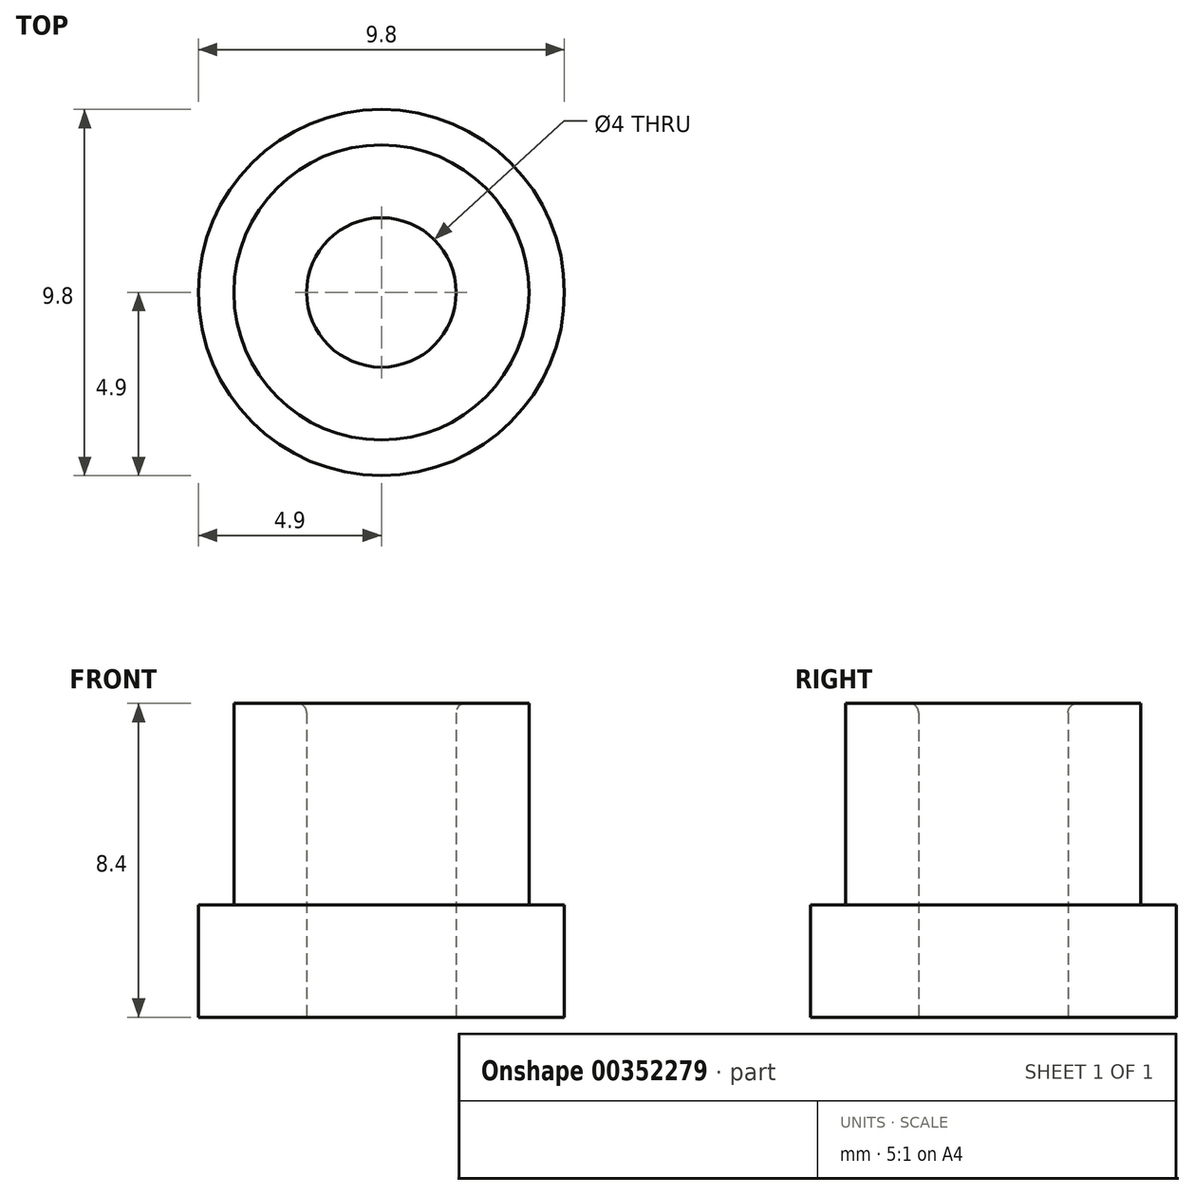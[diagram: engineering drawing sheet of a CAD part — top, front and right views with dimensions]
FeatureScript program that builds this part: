
annotation { "Feature Type Name" : "Feature", "Feature Type Description" : "" }
export const myFeature = defineFeature(function(context is Context, id is Id, definition is map)
    precondition{}
    {
        {
            var Q0;
            Q0=qCreatedBy(makeId("Top.planeOp"),FACE);
            var sketch = newSketch(context, id + "F0", { "sketchPlane" : qUnion([Q0])});
            skCircle(sketch, "E0", {"center": v(0, 0) * mm, "radius": 2 * mm});
            skCircle(sketch, "E1", {"center": v(0, 0) * mm, "radius": 3.95 * mm});
            skCircle(sketch, "E2", {"center": v(0, 0) * mm, "radius": 4.9 * mm});
            skSolve(sketch);
        }
        {
            var Q0;
            Q0=makeQuery(id+"F0.imprint","IMPRINT",FACE,{"disambiguationData":[TD([[makeQuery(id+"F0.imprint","IMPRINT",EDGE,{"derivedFrom":sQuery(id+"F0.wireOp",EDGE,"E1")}),-1.0]])]});
            extrude(context, id + "F1", {"entities" : qUnion([Q0]), "depth" : 3 * mm});
        }
        {
            var Q0;
            Q0=makeQuery(id+"F0.imprint","IMPRINT",FACE,{"disambiguationData":[TD([[makeQuery(id+"F0.imprint","IMPRINT",EDGE,{"derivedFrom":sQuery(id+"F0.wireOp",EDGE,"E0")}),-1.0]])]});
            extrude(context, id + "F2", {"entities" : qUnion([Q0]), "operationType" : NewBodyOperationType.ADD, "depth" : 8.4 * mm});
        }
        {
            var Q0;
            Q0=makeQuery(id+"F2.opExtrude","CAP_EDGE",EDGE,{"disambiguationData":[OSD([sQuery(id+"F0.wireOp",EDGE,"E0")])],"isStart":false});
            fillet(context, id + "F3", {"entities" : qUnion([Q0]), "radius" : .25 * mm, "tangentPropagation" : true, "allowEdgeOverflow" : false});
        }
    });
